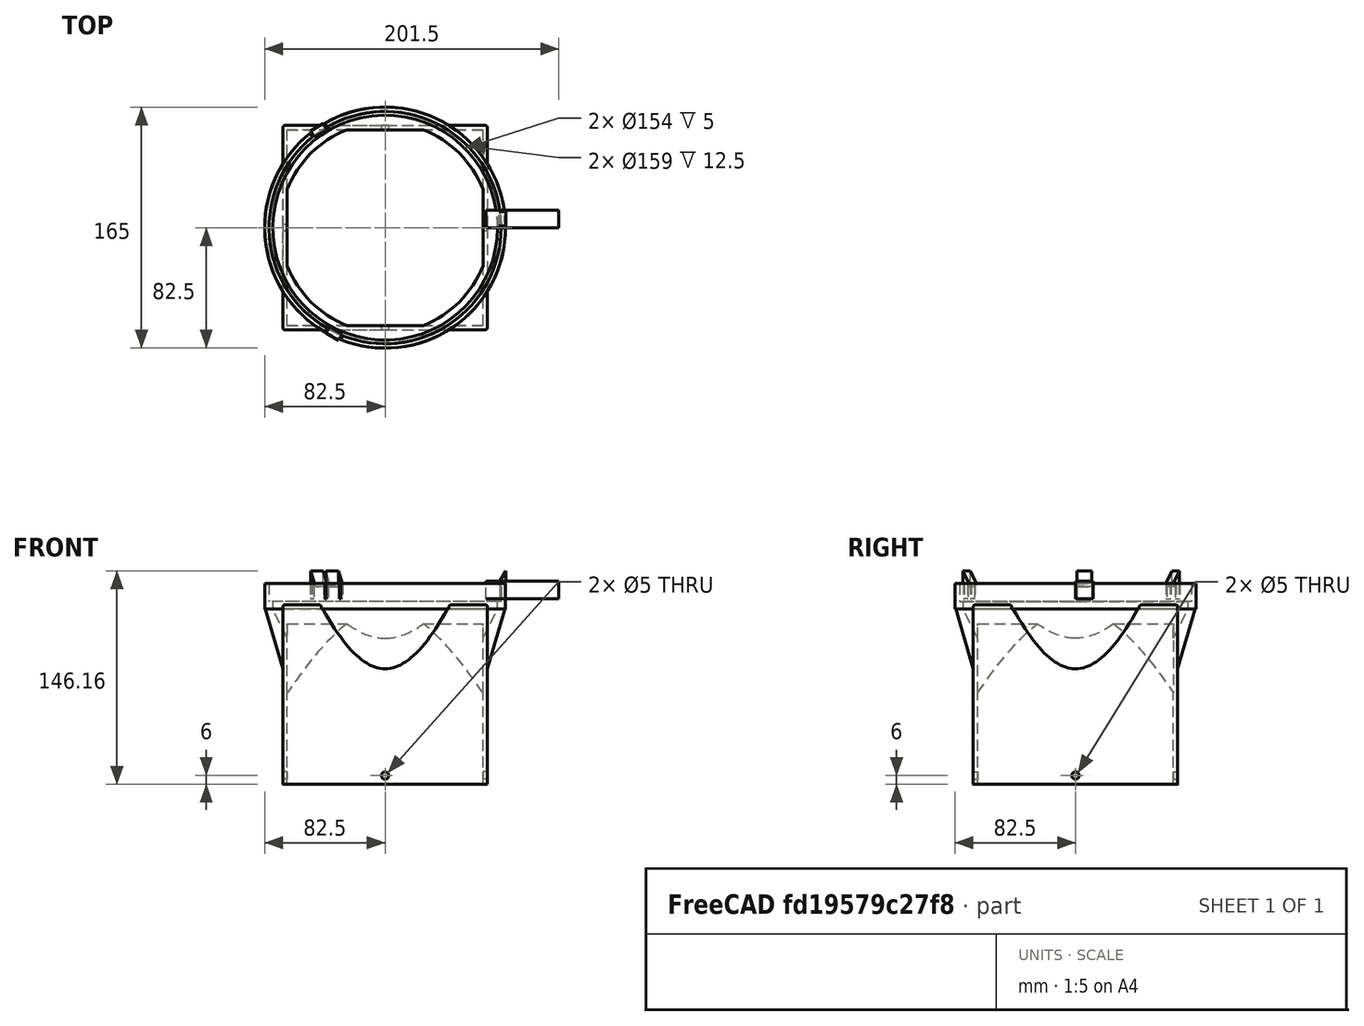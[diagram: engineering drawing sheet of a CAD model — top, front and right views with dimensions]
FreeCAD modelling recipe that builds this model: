
FCSTD DOCUMENT  (FreeCAD 1.0R1.0.0)
Label: Monoblock Pipe Hose to Rect Feedthrough
License: All rights reserved
LicenseURL: http://en.wikipedia.org/wiki/All_rights_reserved
objects: Part::Cylinder×11, Part::MultiFuse×9, Part::Box×8, Part::Cut×8, Part::Cone×4, Spreadsheet::Sheet×3, Part::FeaturePython×2, Part::MultiCommon×2, Part::Fillet×1, Part::Compound×1
note: 44 computed .brp shape members not serialized (recipe doc carries the construction recipe); baked Part::Feature solids carry a one-line shape summary decoded from their .brp

FEATURE [Spreadsheet::Sheet] Spreadsheet
  cells = A2='Rectangular section outer length; B2(rect_l)=140; A3='Rectangular section length; B3(rect_h)=100; A4='Interface length; B4(iflen)=20
FEATURE [Part::Box] Box  label="Cube"
  AttacherType = Attacher::AttachEngine3D
  Height = 12
  Length = 50
  Placement = pos=(69,0,7) rot=(0,0,1;0rad)
  Width = 12
  expr: .Placement.Base.x = <<ACHoseAdapter>>.hose_od / 2 - 10
  expr: .Placement.Base.z = <<ACHoseAdapter>>.addendum + 2
  expr: Height = <<ACHoseAdapter>>.clamp_depth
  expr: Width = 10 + 2
FEATURE [Part::FeaturePython] Array  # Draft array (typed FeaturePython)
  AlwaysSyncPlacement = false
  Angle = 360
  ArrayType = 1
  Axis = (0,0,1)
  Base = -> Box
  Center = (0,0,0)
  Count = 3
  ExpandArray = false
  Fuse = false
  IntervalAxis = (0,0,0)
  IntervalX = (50,0,0)
  IntervalY = (0,50,0)
  IntervalZ = (0,0,50)
  NumberCircles = 3
  NumberPolar = 3
  NumberX = 2
  NumberY = 2
  NumberZ = 1
  PlacementList = 3 placements: [(69,0,7),(-34.5,59.7558,7),(-34.5,-59.7558,7)]
  RadialDistance = 50
  ScaleList = (3) [(1,1,1),(1,1,1),(1,1,1)]
  Symmetry = 1
  TangentialDistance = 25
FEATURE [Part::Box] Box001  label="Cube001"
  AttacherType = Attacher::AttachEngine3D
  Height = 12
  Length = 5
  Placement = pos=(77.8,1,7) rot=(0,0,1;0rad)
  Width = 10
  expr: .Placement.Base.x = <<ACHoseAdapter>>.hose_od / 2 - <<ACHoseAdapter>>.clamp_inset
  expr: .Placement.Base.z = <<ACHoseAdapter>>.addendum + 2
  expr: Height = <<ACHoseAdapter>>.clamp_depth
  expr: Width = 10
FEATURE [Part::Box] Box002  label="Cube002"
  AttacherType = Attacher::AttachEngine3D
  Height = 12
  Length = 5
  Placement = pos=(77.8,1,17.5) rot=(0,0,1;0rad)
  Width = 10
  expr: .Placement.Base.x = <<ACHoseAdapter>>.hose_od / 2 - <<ACHoseAdapter>>.clamp_inset
  expr: .Placement.Base.z = <<ACHoseAdapter>>.addendum + <<ACHoseAdapter>>.clamp_depth + <<ACHoseAdapter>>.tolerance
  expr: Height = <<ACHoseAdapter>>.clamp_depth
  expr: Width = 10
FEATURE [Part::Box] Box003  label="Cube003"
  AttacherType = Attacher::AttachEngine3D
  Height = 12
  Length = 5
  Placement = pos=(77.8,1,17.5) rot=(0,1,0;0.523599rad)
  Width = 10
  expr: .Placement.Base.x = <<ACHoseAdapter>>.hose_od / 2 - <<ACHoseAdapter>>.clamp_inset
  expr: .Placement.Base.z = <<ACHoseAdapter>>.addendum + <<ACHoseAdapter>>.clamp_depth + <<ACHoseAdapter>>.tolerance
  expr: Height = <<ACHoseAdapter>>.clamp_depth
  expr: Width = 10
FEATURE [Part::MultiCommon] Common001
  Shapes = -> [Box003,Box002]
FEATURE [Part::Cylinder] Cylinder
  Angle = 360
  AttacherType = Attacher::AttachEngine3D
  FirstAngle = 0
  Height = 5
  Radius = 77
  SecondAngle = 0
  expr: Height = <<ACHoseAdapter>>.addendum
  expr: Radius = <<ACHoseAdapter>>.hose_od / 2 - <<ACHoseAdapter>>.clamp_counterareainset
FEATURE [Part::Cylinder] Cylinder001
  Angle = 360
  AttacherType = Attacher::AttachEngine3D
  FirstAngle = 0
  Height = 12.5
  Placement = pos=(0,0,5) rot=(0,0,1;0rad)
  Radius = 79.5
  SecondAngle = 0
  expr: .Placement.Base.z = <<ACHoseAdapter>>.addendum
  expr: Height = <<ACHoseAdapter>>.clamp_depth + <<ACHoseAdapter>>.tolerance
  expr: Radius = <<ACHoseAdapter>>.hose_od / 2 + <<ACHoseAdapter>>.tolerance
FEATURE [Part::Cylinder] Cylinder002
  Angle = 360
  AttacherType = Attacher::AttachEngine3D
  FirstAngle = 0
  Height = 17.5
  Radius = 82.5
  SecondAngle = 0
  expr: Height = <<ACHoseAdapter>>.clamp_depth + <<ACHoseAdapter>>.tolerance + <<ACHoseAdapter>>.addendum
  expr: Radius = <<ACHoseAdapter>>.hose_od / 2 + <<ACHoseAdapter>>.tolerance + <<ACHoseAdapter>>.wallthickness
FEATURE [Part::Cylinder] Cylinder003
  Angle = 360
  AttacherType = Attacher::AttachEngine3D
  FirstAngle = 0
  Height = 17.5
  Radius = 79.5
  SecondAngle = 0
  expr: .Placement.Base.z = 0
  expr: Height = <<ACHoseAdapter>>.clamp_depth + <<ACHoseAdapter>>.tolerance + <<ACHoseAdapter>>.addendum
  expr: Radius = <<ACHoseAdapter>>.hose_od / 2 + <<ACHoseAdapter>>.tolerance
FEATURE [Part::Cylinder] Cylinder004
  Angle = 360
  AttacherType = Attacher::AttachEngine3D
  FirstAngle = 0
  Height = 17.5
  Radius = 82.5
  SecondAngle = 0
  expr: Height = <<ACHoseAdapter>>.clamp_depth + <<ACHoseAdapter>>.tolerance + <<ACHoseAdapter>>.addendum
  expr: Radius = <<ACHoseAdapter>>.hose_od / 2 + <<ACHoseAdapter>>.tolerance + <<ACHoseAdapter>>.wallthickness
FEATURE [Part::Cut] Cut001
  Base = -> Cylinder004
  Tool = -> Cylinder003
FEATURE [Part::MultiCommon] Common
  Shapes = -> [Box001,Cut001]
FEATURE [Part::Cylinder] Cylinder005
  Angle = 360
  AttacherType = Attacher::AttachEngine3D
  FirstAngle = 0
  Height = 5
  Radius = 77
  SecondAngle = 0
  expr: Height = <<ACHoseAdapter>>.addendum
  expr: Radius = <<ACHoseAdapter>>.hose_od / 2 - <<ACHoseAdapter>>.clamp_counterareainset
FEATURE [Part::Cylinder] Cylinder006
  Angle = 360
  AttacherType = Attacher::AttachEngine3D
  FirstAngle = 0
  Height = 12.5
  Placement = pos=(0,0,5) rot=(0,0,1;0rad)
  Radius = 79.5
  SecondAngle = 0
  expr: .Placement.Base.z = <<ACHoseAdapter>>.addendum
  expr: Height = <<ACHoseAdapter>>.clamp_depth + <<ACHoseAdapter>>.tolerance
  expr: Radius = <<ACHoseAdapter>>.hose_od / 2 + <<ACHoseAdapter>>.tolerance
FEATURE [Part::Cylinder] Cylinder007
  Angle = 360
  AttacherType = Attacher::AttachEngine3D
  FirstAngle = 0
  Height = 17.5
  Radius = 82.5
  SecondAngle = 0
  expr: Height = <<ACHoseAdapter>>.clamp_depth + <<ACHoseAdapter>>.tolerance + <<ACHoseAdapter>>.addendum
  expr: Radius = <<ACHoseAdapter>>.hose_od / 2 + <<ACHoseAdapter>>.tolerance + <<ACHoseAdapter>>.wallthickness
FEATURE [Part::MultiFuse] Fusion
  Shapes = -> [Cylinder001,Cylinder]
FEATURE [Part::Cut] Cut  label="AttachmentSeatRecess_NoClamps"
  Base = -> Cylinder002
  Tool = -> Fusion
FEATURE [Part::MultiFuse] Fusion002
  Shapes = -> [Cylinder006,Cylinder005]
FEATURE [Part::Cut] Cut002  label="AttachmentSeatRecess_NoClamps001"
  Base = -> Cylinder007
  Tool = -> Fusion002
FEATURE [Part::Cut] Cut003
  Base = -> Cut002
  Tool = -> Array
FEATURE [Spreadsheet::Sheet] Spreadsheet001  label="ACHoseAdapter"
  cells = A1='Model setting; E1='Calculated properties; A2='Hose OD; B2(hose_od)=158; C2='Outer diameter of the hose; E2='Flow cross section; F2(crosssect_flow)==hose_id / 2 * pi; G2='The cross section for airflow. In optimal case keep constant; A3='Hose ID; B3(hose_id)=120; C3='Used for cross section calculations (Note: Estimated at the moment); A4='Hose clamp depth; B4(clamp_depth)=12; C4='Depth of clamping space; A5='Counter diameter; B5(clamp_counterareainset)=2; C5='Area on which the hose is pushed against; A6='Clamp inset; B6(clamp_inset)=1.2; C6='Distance the clamps go inwards into the hose section; A7='Adjustable settings; A8='Tolerance; B8(tolerance)=0.5; C8='Add this tolerance to all spacings; A9='Attachment Thickness; B9(addendum)=5; C9='This is the area the model extends to the bottom to attach to other models; A10='Wall thickness; B10(wallthickness)=3; C10='Thickness of the PLA walls
FEATURE [Part::Box] Box004  label="Cube004"
  AttacherType = Attacher::AttachEngine3D
  Height = 123
  Length = 140
  Placement = pos=(-70,-70,-120) rot=(0,0,1;0rad)
  Width = 140
  expr: .Placement.Base.x = -Spreadsheet.rect_l / 2
  expr: .Placement.Base.y = -Spreadsheet.rect_l / 2
  expr: .Placement.Base.z = -Spreadsheet.rect_h - Spreadsheet.iflen
  expr: Height = Spreadsheet.rect_h + Spreadsheet.iflen + <<ACHoseAdapter>>.wallthickness
  expr: Length = Spreadsheet.rect_l
  expr: Width = Spreadsheet.rect_l
FEATURE [Part::Box] Box005  label="Cube005"
  AttacherType = Attacher::AttachEngine3D
  Height = 120
  Length = 134
  Placement = pos=(-67,-67,-120) rot=(0,0,1;0rad)
  Width = 134
  expr: .Placement.Base.x = -(Spreadsheet.rect_l - <<ACHoseAdapter>>.wallthickness * 2) / 2
  expr: .Placement.Base.y = -(Spreadsheet.rect_l - <<ACHoseAdapter>>.wallthickness * 2) / 2
  expr: .Placement.Base.z = -Spreadsheet.rect_h - Spreadsheet.iflen
  expr: Height = Spreadsheet.rect_h + Spreadsheet.iflen
  expr: Length = Spreadsheet.rect_l - <<ACHoseAdapter>>.wallthickness * 2
  expr: Width = Spreadsheet.rect_l - <<ACHoseAdapter>>.wallthickness * 2
FEATURE [Part::Cone] Cone
  Angle = 360
  AttacherType = Attacher::AttachEngine3D
  Height = 41
  Placement = pos=(0,0,-41) rot=(0,0,1;0rad)
  Radius1 = 70
  Radius2 = 82
  expr: .Placement.Base.z = -max(Spreadsheet.iflen; (<<ACHoseAdapter>>.hose_od / 2 + <<ACHoseAdapter>>.wallthickness) / 2)
  expr: Height = max(Spreadsheet.iflen; (<<ACHoseAdapter>>.hose_od / 2 + <<ACHoseAdapter>>.wallthickness) / 2)
  expr: Radius1 = Spreadsheet.rect_l / 2
  expr: Radius2 = <<ACHoseAdapter>>.hose_od / 2 + <<ACHoseAdapter>>.wallthickness
FEATURE [Part::Cone] Cone001
  Angle = 360
  AttacherType = Attacher::AttachEngine3D
  Height = 20
  Placement = pos=(0,0,-20) rot=(0,0,1;0rad)
  Radius1 = 67
  Radius2 = 77
  expr: .Placement.Base.z = -Spreadsheet.iflen
  expr: Height = Spreadsheet.iflen
  expr: Radius1 = Spreadsheet.rect_l / 2 - <<ACHoseAdapter>>.wallthickness
  expr: Radius2 = <<ACHoseAdapter001>>.hose_od / 2 - <<ACHoseAdapter>>.clamp_counterareainset
FEATURE [Spreadsheet::Sheet] Spreadsheet002  label="ACHoseAdapter001"
  cells = A1='Model setting; E1='Calculated properties; A2='Hose OD; B2(hose_od)=158; C2='Outer diameter of the hose; E2='Flow cross section; F2(crosssect_flow)==hose_id / 2 * pi; G2='The cross section for airflow. In optimal case keep constant; A3='Hose ID; B3(hose_id)=120; C3='Used for cross section calculations (Note: Estimated at the moment); A4='Hose clamp depth; B4(clamp_depth)=12; C4='Depth of clamping space; A5='Counter diameter; B5(clamp_counterareainset)=2; C5='Area on which the hose is pushed against; A6='Clamp inset; B6(clamp_inset)=1.2; C6='Distance the clamps go inwards into the hose section; A7='Adjustable settings; A8='Tolerance; B8(tolerance)=0.5; C8='Add this tolerance to all spacings; A9='Attachment Thickness; B9(addendum)=5; C9='This is the area the model extends to the bottom to attach to other models; A10='Wall thickness; B10(wallthickness)=3; C10='Thickness of the PLA walls
FEATURE [Part::MultiFuse] Fusion004
  Shapes = -> [Cone,Box004]
FEATURE [Part::Cylinder] Cylinder008
  Angle = 360
  AttacherType = Attacher::AttachEngine3D
  FirstAngle = 0
  Height = 3
  Radius = 77
  SecondAngle = 0
  expr: Height = <<ACHoseAdapter>>.wallthickness
  expr: Radius = <<ACHoseAdapter>>.hose_od / 2 - <<ACHoseAdapter>>.clamp_counterareainset
FEATURE [Part::MultiFuse] Fusion005
  Shapes = -> [Box005,Cone001,Cylinder008]
FEATURE [Part::Cut] Cut004
  Base = -> Fusion004
  Tool = -> Fusion005
FEATURE [Part::Fillet] Fillet
  Base = -> Cut004
  EdgeLinks = -> Cut004 [Edge6,Edge11,Edge12,Edge14,Edge18,Edge28,Edge34,Edge35,Edge48,Edge49,Edge70,Edge71]
  Edges = 12 edges r=1.5: [Edge6,Edge11,Edge12,Edge14,Edge18,Edge28,Edge34,Edge35,Edge48,Edge49,Edge70,Edge71]
FEATURE [Part::Cylinder] Cylinder009
  Angle = 360
  AttacherType = Attacher::AttachEngine3D
  FirstAngle = 0
  Height = 140
  Placement = pos=(0,70,-114) rot=(1,0,0;1.5708rad)
  Radius = 2.5
  SecondAngle = 0
  expr: .Placement.Base.y = Spreadsheet.rect_l / 2
  expr: .Placement.Base.z = -Spreadsheet.rect_h - Spreadsheet.iflen + 6
  expr: Height = Spreadsheet.rect_l
FEATURE [Part::Cylinder] Cylinder010
  Angle = 360
  AttacherType = Attacher::AttachEngine3D
  FirstAngle = 0
  Height = 140
  Placement = pos=(0,70,-114) rot=(1,0,0;1.5708rad)
  Radius = 2.5
  SecondAngle = 0
  expr: .Placement.Base.y = Spreadsheet.rect_l / 2
  expr: .Placement.Base.z = -Spreadsheet.rect_h - Spreadsheet.iflen + 6
  expr: Height = Spreadsheet.rect_l
FEATURE [Part::Compound] Compound
  Links = -> [Cylinder010]
  Placement = pos=(0,0,0) rot=(0,0,1;1.5708rad)
FEATURE [Part::MultiFuse] Fusion006
  Shapes = -> [Compound,Cylinder009]
FEATURE [Part::Cut] Cut005
  Base = -> Fillet
  Tool = -> Fusion006
FEATURE [Part::Cone] Cone002
  Angle = 360
  AttacherType = Attacher::AttachEngine3D
  Height = 60
  Placement = pos=(0,0,-20) rot=(0,0,1;0rad)
  Radius1 = 95.9949
  Radius2 = 67
  expr: .Placement.Base.z = -Spreadsheet.iflen
  expr: Height = 3 * Spreadsheet.iflen
  expr: Radius1 = Spreadsheet.rect_l * sqrt(2) / 2 - <<ACHoseAdapter>>.wallthickness
  expr: Radius2 = Spreadsheet.rect_l / 2 - <<ACHoseAdapter>>.wallthickness
FEATURE [Part::Box] Box006  label="Cube006"
  AttacherType = Attacher::AttachEngine3D
  Height = 60
  Length = 134
  Placement = pos=(-67,-67,-20) rot=(0,0,1;0rad)
  Width = 134
  expr: .Placement.Base.x = -(Spreadsheet.rect_l - <<ACHoseAdapter>>.wallthickness * 2) / 2
  expr: .Placement.Base.y = -(Spreadsheet.rect_l - <<ACHoseAdapter>>.wallthickness * 2) / 2
  expr: .Placement.Base.z = -Spreadsheet.iflen
  expr: Height = 3 * Spreadsheet.iflen
  expr: Length = Spreadsheet.rect_l - <<ACHoseAdapter>>.wallthickness * 2
  expr: Width = Spreadsheet.rect_l - <<ACHoseAdapter>>.wallthickness * 2
FEATURE [Part::Cut] Cut006
  Base = -> Box006
  Placement = pos=(0,0,-40) rot=(0,0,1;0rad)
  Tool = -> Cone002
  expr: .Placement.Base.z = -2 * Spreadsheet.iflen
FEATURE [Part::Cone] Cone003
  Angle = 360
  AttacherType = Attacher::AttachEngine3D
  Height = 20
  Placement = pos=(0,0,-20) rot=(0,0,1;0rad)
  Radius1 = 67
  Radius2 = 77
  expr: .Placement.Base.z = -Spreadsheet.iflen
  expr: Height = Spreadsheet.iflen
  expr: Radius1 = Spreadsheet.rect_l / 2 - <<ACHoseAdapter>>.wallthickness
  expr: Radius2 = <<ACHoseAdapter001>>.hose_od / 2 - <<ACHoseAdapter>>.clamp_counterareainset
FEATURE [Part::Cut] Cut007
  Base = -> Cut006
  Tool = -> Cone003
FEATURE [Part::Box] Box007  label="Cube007"
  AttacherType = Attacher::AttachEngine3D
  Height = 2
  Length = 2.5
  Placement = pos=(77.8,1,17.5) rot=(0,1,0;1.0472rad)
  Width = 10
  expr: .Placement.Base.x = <<ACHoseAdapter>>.hose_od / 2 - <<ACHoseAdapter>>.clamp_inset
  expr: .Placement.Base.z = <<ACHoseAdapter>>.addendum + <<ACHoseAdapter>>.clamp_depth + <<ACHoseAdapter>>.tolerance
  expr: Height = 2
  expr: Width = 10
FEATURE [Part::MultiFuse] Fusion001  label="ClampSingle"
  Shapes = -> [Common,Common001,Box007]
FEATURE [Part::FeaturePython] Array001  # Draft array (typed FeaturePython)
  AlwaysSyncPlacement = false
  Angle = 360
  ArrayType = 1
  Axis = (0,0,1)
  Base = -> Fusion001
  Center = (0,0,0)
  Count = 3
  ExpandArray = false
  Fuse = false
  IntervalAxis = (0,0,0)
  IntervalX = (50,0,0)
  IntervalY = (0,50,0)
  IntervalZ = (0,0,50)
  NumberCircles = 3
  NumberPolar = 3
  NumberX = 2
  NumberY = 2
  NumberZ = 1
  PlacementList = 3 placements: [(0,0,0),(0,0,0),(0,0,0)]
  RadialDistance = 50
  ScaleList = (3) [(1,1,1),(1,1,1),(1,1,1)]
  Symmetry = 1
  TangentialDistance = 25
FEATURE [Part::MultiFuse] Fusion003
  Shapes = -> [Cut003,Array001]
FEATURE [Part::MultiFuse] Fusion007
  Shapes = -> [Cut005,Fusion003]
FEATURE [Part::MultiFuse] Fusion008
  Shapes = -> [Fusion007,Cut007]
